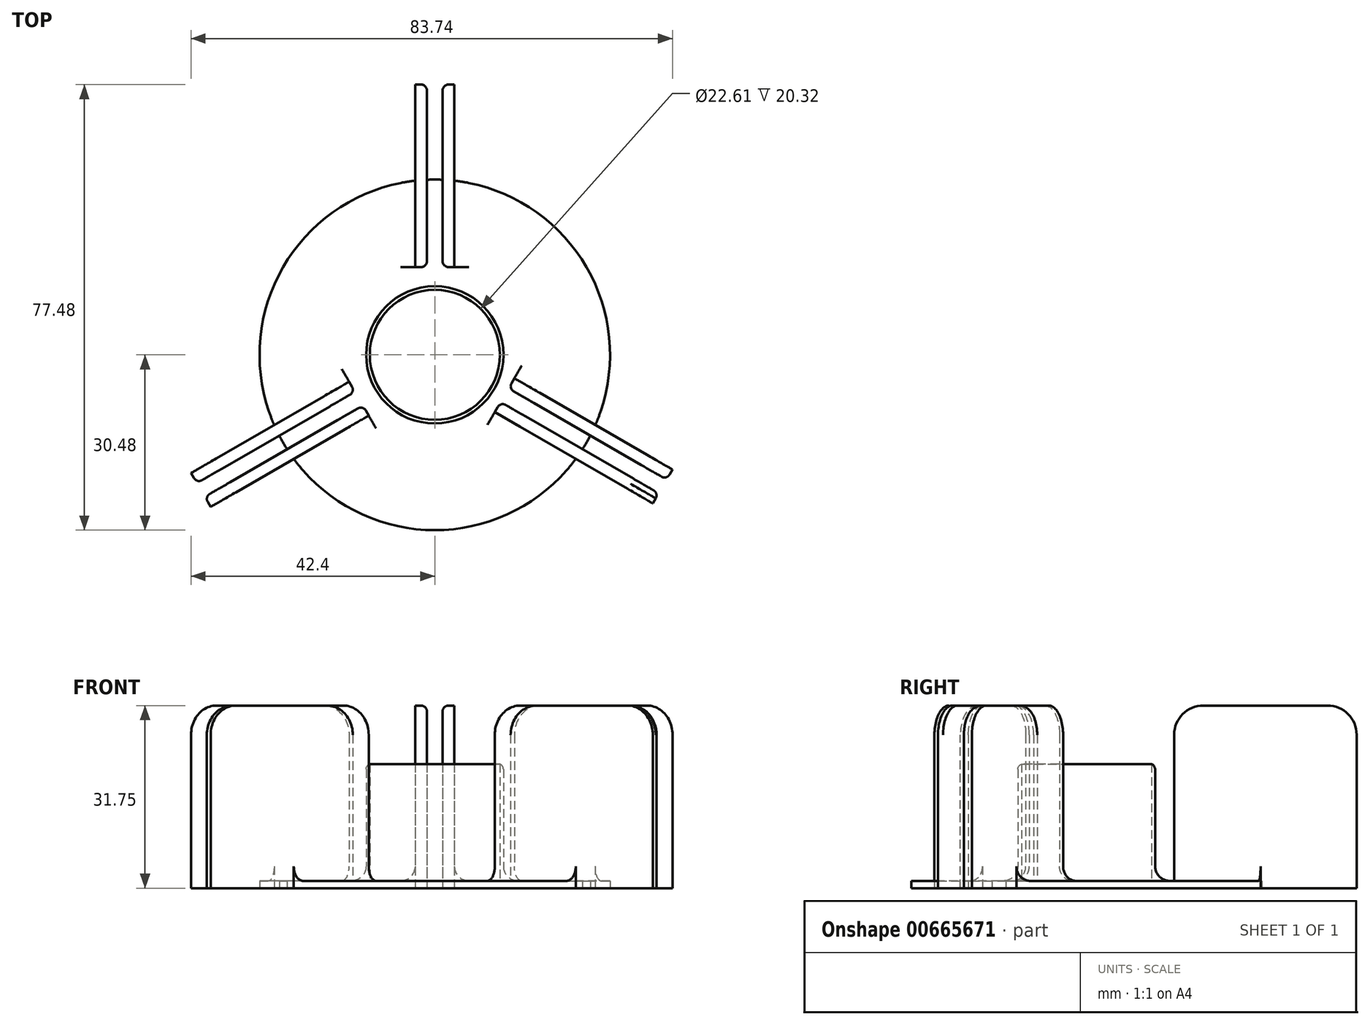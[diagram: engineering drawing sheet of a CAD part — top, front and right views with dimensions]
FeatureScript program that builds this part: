
annotation { "Feature Type Name" : "Feature", "Feature Type Description" : "" }
export const myFeature = defineFeature(function(context is Context, id is Id, definition is map)
    precondition{}
    {
        {
            var Q0;
            Q0=qCreatedBy(makeId("Top.planeOp"),FACE);
            var sketch = newSketch(context, id + "F0", { "sketchPlane" : qUnion([Q0])});
            skCircle(sketch, "E0", {"center": v(0, 0) * mm, "radius": 12.55 * mm});
            skCircle(sketch, "E1", {"center": v(0, 0) * mm, "radius": 30.48 * mm});
            skSolve(sketch);
        }
        {
            var Q0;
            Q0=makeQuery(id+"F0.imprint","IMPRINT",FACE,{"disambiguationData":[TD([[makeQuery(id+"F0.imprint","IMPRINT",EDGE,{"derivedFrom":sQuery(id+"F0.wireOp",EDGE,"E0")}),-1.0]])]});
            var Q1;
            Q1=makeQuery(id+"F0.imprint","IMPRINT",FACE,{"disambiguationData":[TD([[makeQuery(id+"F0.imprint","IMPRINT",EDGE,{"derivedFrom":sQuery(id+"F0.wireOp",EDGE,"E0")}),1.0]])]});
            extrude(context, id + "F1", {"entities" : qUnion([Q0, Q1]), "depth" : 1.27 * mm, "offsetDistance" : 25.4 * mm});
        }
        {
            var Q0;
            Q0=qCreatedBy(makeId("Top.planeOp"),FACE);
            var sketch = newSketch(context, id + "F2", { "sketchPlane" : qUnion([Q0])});
            skPoint(sketch, "E2", {"position": v(0, 42.13) * mm});
            skPoint(sketch, "E3", {"position": v(36.63, -21.15) * mm});
            skPoint(sketch, "E4", {"position": v(-36.99, -21.35) * mm});
            skLineSegment(sketch, "E5", {"start": v(0, 0) * mm, "end": v(0, 42.13) * mm});
            skLineSegment(sketch, "E6", {"start": v(0, 0) * mm, "end": v(36.63, -21.15) * mm});
            skLineSegment(sketch, "E7", {"start": v(0, 0) * mm, "end": v(-36.99, -21.35) * mm});
            skPoint(sketch, "E8", {"position": v(0, 15.24) * mm});
            skPoint(sketch, "E9", {"position": v(0, 22.86) * mm});
            skLineSegment(sketch, "E10.left", {"start": v(-1.37, 47) * mm, "end": v(-1.37, 39.38) * mm});
            skLineSegment(sketch, "E10.right", {"start": v(1.37, 47) * mm, "end": v(1.37, 39.38) * mm});
            skLineSegment(sketch, "E11.bottom", {"start": v(-1.37, 47) * mm, "end": v(-3.4, 47) * mm});
            skLineSegment(sketch, "E11.top", {"start": v(-1.37, 15.25) * mm, "end": v(-3.4, 15.25) * mm});
            skLineSegment(sketch, "E11.left", {"start": v(-1.37, 47) * mm, "end": v(-1.37, 15.25) * mm});
            skLineSegment(sketch, "E11.right", {"start": v(-3.4, 47) * mm, "end": v(-3.4, 15.25) * mm});
            skLineSegment(sketch, "E12.bottom", {"start": v(1.37, 47) * mm, "end": v(3.4, 47) * mm});
            skLineSegment(sketch, "E12.top", {"start": v(1.37, 15.25) * mm, "end": v(3.4, 15.25) * mm});
            skLineSegment(sketch, "E12.left", {"start": v(1.37, 47) * mm, "end": v(1.37, 15.25) * mm});
            skLineSegment(sketch, "E12.right", {"start": v(3.4, 47) * mm, "end": v(3.4, 15.25) * mm});
            skPoint(sketch, "E13", {"position": v(12.14, -7.01) * mm});
            skPoint(sketch, "E14", {"position": v(19.79, -11.45) * mm});
            skLineSegment(sketch, "E15.left", {"start": v(40.33, -21.7) * mm, "end": v(32.67, -17.28) * mm});
            skLineSegment(sketch, "E15.right", {"start": v(38.95, -24.07) * mm, "end": v(11.45, -8.2) * mm});
            skLineSegment(sketch, "E16.bottom", {"start": v(40.33, -21.7) * mm, "end": v(41.34, -19.94) * mm});
            skLineSegment(sketch, "E16.top", {"start": v(12.83, -5.82) * mm, "end": v(13.85, -4.07) * mm});
            skLineSegment(sketch, "E16.left", {"start": v(40.33, -21.7) * mm, "end": v(12.83, -5.82) * mm});
            skLineSegment(sketch, "E16.right", {"start": v(41.34, -19.94) * mm, "end": v(13.85, -4.07) * mm});
            skLineSegment(sketch, "E17.bottom", {"start": v(38.95, -24.07) * mm, "end": v(37.93, -25.83) * mm});
            skLineSegment(sketch, "E17.left", {"start": v(38.95, -24.07) * mm, "end": v(31.3, -19.63) * mm});
            skPoint(sketch, "E18", {"position": v(-13.2, -7.62) * mm});
            skLineSegment(sketch, "E19.bottom", {"start": v(-40, -24.68) * mm, "end": v(-39, -26.44) * mm});
            skLineSegment(sketch, "E19.top", {"start": v(-12.51, -8.8) * mm, "end": v(-11.5, -10.57) * mm});
            skLineSegment(sketch, "E19.left", {"start": v(-40, -24.68) * mm, "end": v(-12.51, -8.8) * mm});
            skLineSegment(sketch, "E19.right", {"start": v(-39, -26.44) * mm, "end": v(-11.5, -10.57) * mm});
            skLineSegment(sketch, "E20.bottom", {"start": v(-41.38, -22.3) * mm, "end": v(-42.4, -20.55) * mm});
            skLineSegment(sketch, "E20.top", {"start": v(-13.88, -6.43) * mm, "end": v(-14.9, -4.67) * mm});
            skLineSegment(sketch, "E20.left", {"start": v(-41.38, -22.3) * mm, "end": v(-13.88, -6.43) * mm});
            skLineSegment(sketch, "E20.right", {"start": v(-42.4, -20.55) * mm, "end": v(-14.9, -4.67) * mm});
            skLineSegment(sketch, "E21", {"start": v(11.45, -8.2) * mm, "end": v(10.44, -9.96) * mm});
            skLineSegment(sketch, "E22", {"start": v(10.44, -9.96) * mm, "end": v(37.93, -25.83) * mm});
            skSolve(sketch);
        }
        {
            var Q0;
            Q0 = qSketchRegion(id + "F2", true);
            extrude(context, id + "F3", {"entities" : qUnion([Q0]), "operationType" : NewBodyOperationType.ADD, "depth" : 31.75 * mm, "offsetDistance" : 25.4 * mm});
        }
        {
            var Q0;
            Q0=qCreatedBy(makeId("Top.planeOp"),FACE);
            var sketch = newSketch(context, id + "F4", { "sketchPlane" : qUnion([Q0])});
            skCircle(sketch, "E23", {"center": v(0, 0) * mm, "radius": 11.94 * mm});
            skCircle(sketch, "E24", {"center": v(0, 0) * mm, "radius": 11.3 * mm});
            skSolve(sketch);
        }
        {
            var Q0;
            Q0 = qSketchRegion(id + "F4", true);
            extrude(context, id + "F5", {"entities" : qUnion([Q0]), "operationType" : NewBodyOperationType.ADD, "depth" : 21.59 * mm, "offsetDistance" : 25.4 * mm});
        }
        {
            var Q0;
            Q0=makeQuery(id+"F3.opExtrude","CAP_EDGE",EDGE,{"disambiguationData":[OSD([sQuery(id+"F2.wireOp",EDGE,"E19.bottom")])],"isStart":false});
            var Q1;
            Q1=makeQuery(id+"F3.opExtrude","CAP_EDGE",EDGE,{"disambiguationData":[OSD([sQuery(id+"F2.wireOp",EDGE,"E20.bottom")])],"isStart":false});
            var Q2;
            Q2=makeQuery(id+"F3.opExtrude","CAP_EDGE",EDGE,{"disambiguationData":[OSD([sQuery(id+"F2.wireOp",EDGE,"E17.bottom")])],"isStart":false});
            var Q3;
            Q3=makeQuery(id+"F3.opExtrude","CAP_EDGE",EDGE,{"disambiguationData":[OSD([sQuery(id+"F2.wireOp",EDGE,"E11.bottom")])],"isStart":false});
            var Q4;
            Q4=makeQuery(id+"F3.opExtrude","CAP_EDGE",EDGE,{"disambiguationData":[OSD([sQuery(id+"F2.wireOp",EDGE,"E12.bottom")])],"isStart":false});
            var Q5;
            Q5=makeQuery(id+"F3.opExtrude","CAP_EDGE",EDGE,{"disambiguationData":[OSD([sQuery(id+"F2.wireOp",EDGE,"E16.bottom")])],"isStart":false});
            var Q6;
            Q6=makeQuery(id+"F3.opExtrude","CAP_EDGE",EDGE,{"disambiguationData":[OSD([sQuery(id+"F2.wireOp",EDGE,"E12.top")])],"isStart":false});
            var Q7;
            Q7=makeQuery(id+"F3.opExtrude","CAP_EDGE",EDGE,{"disambiguationData":[OSD([sQuery(id+"F2.wireOp",EDGE,"E11.top")])],"isStart":false});
            var Q8;
            Q8=makeQuery(id+"F3.opExtrude","CAP_EDGE",EDGE,{"disambiguationData":[OSD([sQuery(id+"F2.wireOp",EDGE,"E16.top")])],"isStart":false});
            var Q9;
            Q9=makeQuery(id+"F3.opExtrude","CAP_EDGE",EDGE,{"disambiguationData":[OSD([sQuery(id+"F2.wireOp",EDGE,"E19.top")])],"isStart":false});
            var Q10;
            Q10=makeQuery(id+"F3.opExtrude","CAP_EDGE",EDGE,{"disambiguationData":[OSD([sQuery(id+"F2.wireOp",EDGE,"E20.top")])],"isStart":false});
            var Q11;
            Q11=makeQuery(id+"F3.opExtrude","CAP_EDGE",EDGE,{"disambiguationData":[OSD([sQuery(id+"F2.wireOp",EDGE,"E21")])],"isStart":false});
            fillet(context, id + "F6", {"entities" : qUnion([Q0, Q1, Q2, Q3, Q4, Q5, Q6, Q7, Q8, Q9, Q10, Q11]), "radius" : 5.08 * mm, "tangentPropagation" : true, "allowEdgeOverflow" : false});
        }
        {
            var Q0;
            Q0=makeQuery(id+"F3.boolean.opBoolean","INTERSECT",EDGE,{"derivedFrom":[makeQuery(id+"F1.opExtrude","CAP_FACE",FACE,{"disambiguationData":[OSD([sQuery(id+"F0.wireOp",EDGE,"E1")])],"isStart":false}),makeQuery(id+"F3.opExtrude","SWEPT_FACE",FACE,{"disambiguationData":[OSD([sQuery(id+"F2.wireOp",EDGE,"E16.right")])]})]});
            var Q1;
            Q1=makeQuery(id+"F3.boolean.opBoolean","INTERSECT",EDGE,{"derivedFrom":[makeQuery(id+"F1.opExtrude","CAP_FACE",FACE,{"disambiguationData":[OSD([sQuery(id+"F0.wireOp",EDGE,"E1")])],"isStart":false}),makeQuery(id+"F3.opExtrude","SWEPT_FACE",FACE,{"disambiguationData":[OSD([sQuery(id+"F2.wireOp",EDGE,"E12.right")])]})]});
            var Q2;
            Q2=makeQuery(id+"F3.boolean.opBoolean","INTERSECT",EDGE,{"derivedFrom":[makeQuery(id+"F1.opExtrude","CAP_FACE",FACE,{"disambiguationData":[OSD([sQuery(id+"F0.wireOp",EDGE,"E1")])],"isStart":false}),makeQuery(id+"F3.opExtrude","SWEPT_FACE",FACE,{"disambiguationData":[OSD([sQuery(id+"F2.wireOp",EDGE,"E20.right")])]})]});
            var Q3;
            Q3=makeQuery(id+"F3.boolean.opBoolean","INTERSECT",EDGE,{"derivedFrom":[makeQuery(id+"F1.opExtrude","CAP_FACE",FACE,{"disambiguationData":[OSD([sQuery(id+"F0.wireOp",EDGE,"E1")])],"isStart":false}),makeQuery(id+"F3.opExtrude","SWEPT_FACE",FACE,{"disambiguationData":[OSD([sQuery(id+"F2.wireOp",EDGE,"E11.right")])]})]});
            var Q4;
            Q4=makeQuery(id+"F3.boolean.opBoolean","INTERSECT",EDGE,{"derivedFrom":[makeQuery(id+"F1.opExtrude","CAP_FACE",FACE,{"disambiguationData":[OSD([sQuery(id+"F0.wireOp",EDGE,"E1")])],"isStart":false}),makeQuery(id+"F3.opExtrude","SWEPT_FACE",FACE,{"disambiguationData":[OSD([sQuery(id+"F2.wireOp",EDGE,"E19.right")])]})]});
            var Q5;
            Q5=makeQuery(id+"F3.boolean.opBoolean","INTERSECT",EDGE,{"derivedFrom":[makeQuery(id+"F1.opExtrude","CAP_FACE",FACE,{"disambiguationData":[OSD([sQuery(id+"F0.wireOp",EDGE,"E1")])],"isStart":false}),makeQuery(id+"F3.opExtrude","SWEPT_FACE",FACE,{"disambiguationData":[OSD([sQuery(id+"F2.wireOp",EDGE,"E22")])]})]});
            fillet(context, id + "F7", {"entities" : qUnion([Q0, Q1, Q2, Q3, Q4, Q5]), "radius" : 2.54 * mm, "tangentPropagation" : true, "allowEdgeOverflow" : false});
        }
        {
            var Q0;
            Q0=makeQuery(id+"F5.boolean.opBoolean","INTERSECT",EDGE,{"derivedFrom":[makeQuery(id+"F1.opExtrude","CAP_FACE",FACE,{"disambiguationData":[OSD([sQuery(id+"F0.wireOp",EDGE,"E1")])],"isStart":false}),makeQuery(id+"F5.opExtrude","SWEPT_FACE",FACE,{"disambiguationData":[OSD([sQuery(id+"F4.wireOp",EDGE,"E23")])]})]});
            fillet(context, id + "F8", {"entities" : qUnion([Q0]), "radius" : 2.54 * mm, "tangentPropagation" : true, "allowEdgeOverflow" : false});
        }
        {
            var Q0;
            Q0=makeQuery(id+"F3.opExtrude","CAP_EDGE",EDGE,{"disambiguationData":[OSD([sQuery(id+"F2.wireOp",EDGE,"E20.left")])],"isStart":false});
            var Q1;
            Q1=makeQuery(id+"F3.opExtrude","CAP_EDGE",EDGE,{"disambiguationData":[OSD([sQuery(id+"F2.wireOp",EDGE,"E19.left")])],"isStart":false});
            var Q2;
            Q2=makeQuery(id+"F5.opExtrude","CAP_EDGE",EDGE,{"disambiguationData":[OSD([sQuery(id+"F4.wireOp",EDGE,"E23")])],"isStart":false});
            var Q3;
            Q3=makeQuery(id+"F3.opExtrude","CAP_EDGE",EDGE,{"disambiguationData":[OSD([sQuery(id+"F2.wireOp",EDGE,"E16.left")])],"isStart":false});
            var Q4;
            Q4=makeQuery(id+"F3.opExtrude","CAP_EDGE",EDGE,{"disambiguationData":[OSD([sQuery(id+"F2.wireOp",EDGE,"E15.right")])],"isStart":false});
            var Q5;
            Q5=makeQuery(id+"F3.opExtrude","CAP_EDGE",EDGE,{"disambiguationData":[OSD([sQuery(id+"F2.wireOp",EDGE,"E12.left")])],"isStart":false});
            var Q6;
            Q6=makeQuery(id+"F3.opExtrude","CAP_EDGE",EDGE,{"disambiguationData":[OSD([sQuery(id+"F2.wireOp",EDGE,"E11.left")])],"isStart":false});
            fillet(context, id + "F9", {"entities" : qUnion([Q0, Q1, Q2, Q3, Q4, Q5, Q6]), "radius" : 1.02 * mm, "tangentPropagation" : true, "allowEdgeOverflow" : false});
        }
    });
